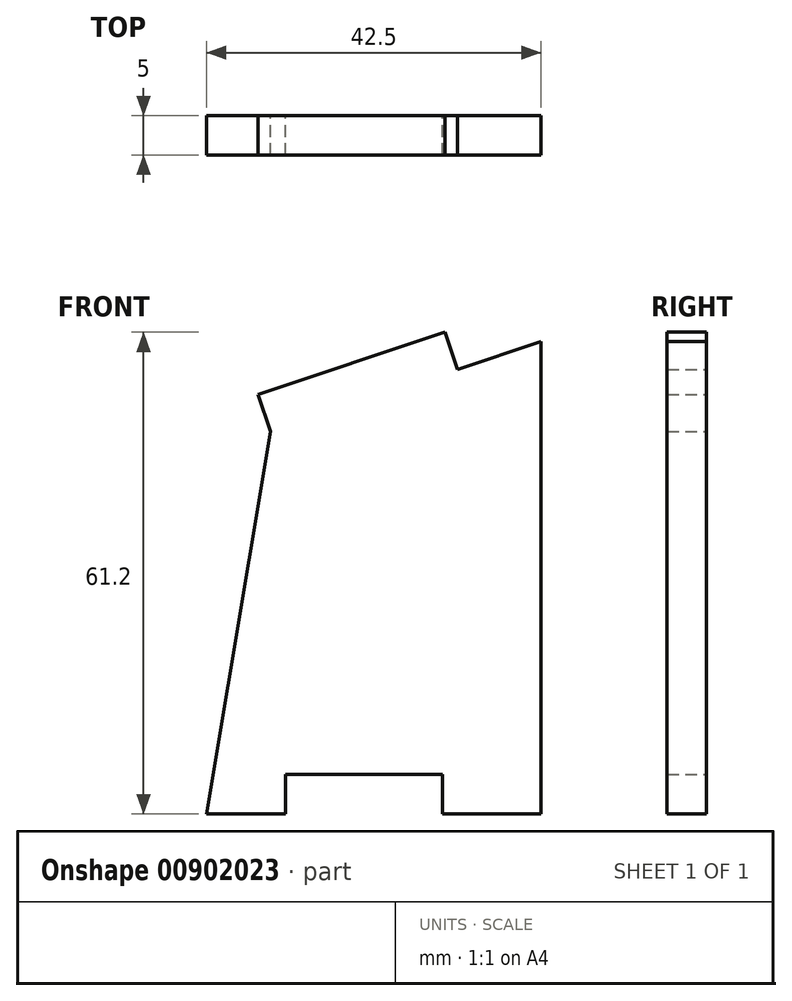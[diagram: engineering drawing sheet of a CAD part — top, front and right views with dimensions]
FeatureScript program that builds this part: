
annotation { "Feature Type Name" : "Feature", "Feature Type Description" : "" }
export const myFeature = defineFeature(function(context is Context, id is Id, definition is map)
    precondition{}
    {
        {
            var Q0;
            Q0=qCreatedBy(makeId("Front.planeOp"),FACE);
            var sketch = newSketch(context, id + "F0", { "sketchPlane" : qUnion([Q0])});
            skLineSegment(sketch, "E0.top", {"start": v(-20, -5) * mm, "end": v(-10, -5) * mm});
            skLineSegment(sketch, "E1", {"start": v(22.5, 55) * mm, "end": v(11.86, 51.45) * mm});
            skLineSegment(sketch, "E2", {"start": v(11.86, 51.45) * mm, "end": v(10.28, 56.2) * mm});
            skLineSegment(sketch, "E3", {"start": v(10.28, 56.2) * mm, "end": v(-13.44, 48.3) * mm});
            skLineSegment(sketch, "E4", {"start": v(-13.44, 48.3) * mm, "end": v(-11.86, 43.55) * mm});
            skLineSegment(sketch, "E5", {"start": v(-10, -5) * mm, "end": v(-10, 0) * mm});
            skLineSegment(sketch, "E6", {"start": v(-10, 0) * mm, "end": v(10, 0) * mm});
            skLineSegment(sketch, "E7", {"start": v(10, 0) * mm, "end": v(10, -5) * mm});
            skLineSegment(sketch, "E8.trimOffspring", {"start": v(10, -5) * mm, "end": v(22.5, -5) * mm});
            skLineSegment(sketch, "E9.trimOffspring", {"start": v(22.5, 55) * mm, "end": v(22.5, -5) * mm});
            skLineSegment(sketch, "E10", {"start": v(-11.86, 43.55) * mm, "end": v(-20, -5) * mm});
            skSolve(sketch);
        }
        {
            var Q0;
            Q0 = qSketchRegion(id + "F0", true);
            extrude(context, id + "F1", {"entities" : qUnion([Q0]), "depth" : 5 * mm, "offsetDistance" : 25 * mm});
        }
    });
